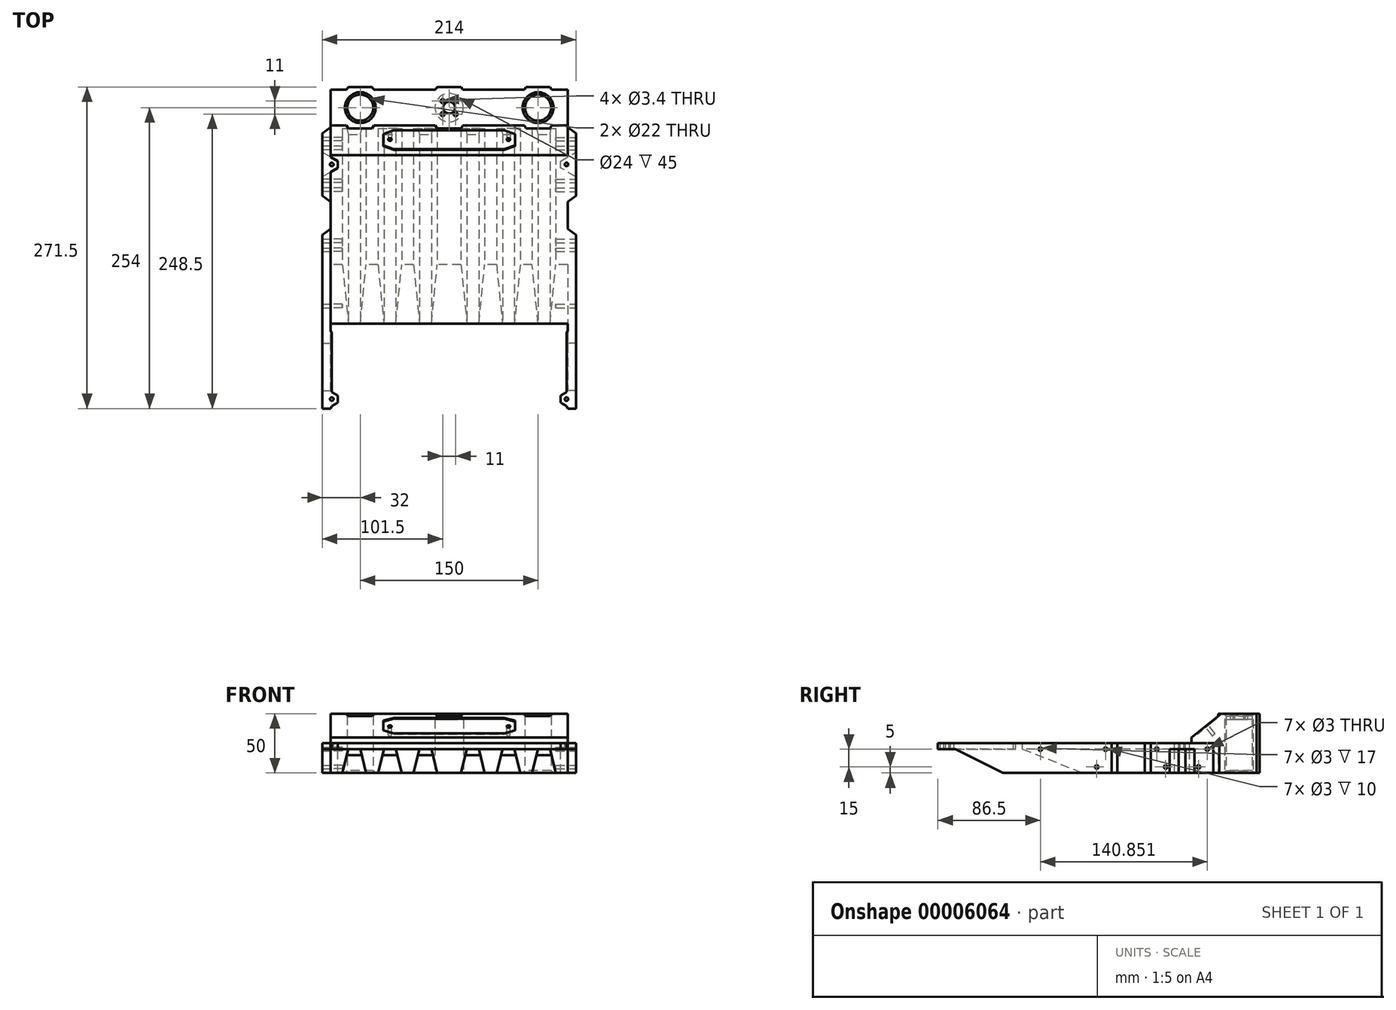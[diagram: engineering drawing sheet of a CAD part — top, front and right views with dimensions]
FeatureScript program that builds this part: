
annotation { "Feature Type Name" : "Feature", "Feature Type Description" : "" }
export const myFeature = defineFeature(function(context is Context, id is Id, definition is map)
    precondition{}
    {
        {
            var Q0;
            Q0=qCreatedBy(makeId("Top.planeOp"),FACE);
            var sketch = newSketch(context, id + "F0", { "sketchPlane" : qUnion([Q0])});
            skLineSegment(sketch, "E0.bottom", {"start": v(0, 0) * mm, "end": v(200, 0) * mm});
            skLineSegment(sketch, "E0.top", {"start": v(0, 30) * mm, "end": v(200, 30) * mm});
            skLineSegment(sketch, "E0.left", {"start": v(0, 0) * mm, "end": v(0, 30) * mm});
            skLineSegment(sketch, "E0.right", {"start": v(200, 0) * mm, "end": v(200, 30) * mm});
            skLineSegment(sketch, "E1", {"start": v(0, 15) * mm, "end": v(200, 15) * mm, "construction": true});
            skLineSegment(sketch, "E2", {"start": v(100, 30) * mm, "end": v(100, 0) * mm, "construction": true});
            skCircle(sketch, "E3", {"center": v(25, 15) * mm, "radius": 11 * mm});
            skCircle(sketch, "E4", {"center": v(175, 15) * mm, "radius": 11 * mm});
            skCircle(sketch, "E5", {"center": v(100, 15) * mm, "radius": 5 * mm});
            skCircle(sketch, "E6.cCircle", {"center": v(25, 15) * mm, "radius": 17.5 * mm, "construction": true});
            skLineSegment(sketch, "E6.0", {"start": v(35.1, -2.5) * mm, "end": v(14.9, -2.5) * mm});
            skLineSegment(sketch, "E6.1", {"start": v(14.9, -2.5) * mm, "end": v(4.8, 15) * mm});
            skLineSegment(sketch, "E6.2", {"start": v(4.8, 15) * mm, "end": v(14.9, 32.5) * mm});
            skLineSegment(sketch, "E6.3", {"start": v(14.9, 32.5) * mm, "end": v(35.1, 32.5) * mm});
            skLineSegment(sketch, "E6.4", {"start": v(35.1, 32.5) * mm, "end": v(45.2, 15) * mm});
            skLineSegment(sketch, "E6.5", {"start": v(45.2, 15) * mm, "end": v(35.1, -2.5) * mm});
            skPoint(sketch, "E6.0.midPoint", {"position": v(25, -2.5) * mm});
            skCircle(sketch, "E7.cCircle", {"center": v(175, 15) * mm, "radius": 17.5 * mm, "construction": true});
            skLineSegment(sketch, "E7.0", {"start": v(164.9, 32.5) * mm, "end": v(185.1, 32.5) * mm});
            skLineSegment(sketch, "E7.1", {"start": v(185.1, 32.5) * mm, "end": v(195.2, 15) * mm});
            skLineSegment(sketch, "E7.2", {"start": v(195.2, 15) * mm, "end": v(185.1, -2.5) * mm});
            skLineSegment(sketch, "E7.3", {"start": v(185.1, -2.5) * mm, "end": v(164.9, -2.5) * mm});
            skLineSegment(sketch, "E7.4", {"start": v(164.9, -2.5) * mm, "end": v(154.8, 15) * mm});
            skLineSegment(sketch, "E7.5", {"start": v(154.8, 15) * mm, "end": v(164.9, 32.5) * mm});
            skPoint(sketch, "E7.0.midPoint", {"position": v(175, 32.5) * mm});
            skLineSegment(sketch, "E8.rect.bottom", {"start": v(94.5, 20.5) * mm, "end": v(105.5, 20.5) * mm, "construction": true});
            skLineSegment(sketch, "E8.rect.top", {"start": v(94.5, 9.5) * mm, "end": v(105.5, 9.5) * mm, "construction": true});
            skLineSegment(sketch, "E8.rect.left", {"start": v(94.5, 20.5) * mm, "end": v(94.5, 9.5) * mm, "construction": true});
            skLineSegment(sketch, "E8.rect.right", {"start": v(105.5, 20.5) * mm, "end": v(105.5, 9.5) * mm, "construction": true});
            skCircle(sketch, "E9", {"center": v(94.5, 20.5) * mm, "radius": 1.7 * mm});
            skCircle(sketch, "E10", {"center": v(105.5, 20.5) * mm, "radius": 1.7 * mm});
            skCircle(sketch, "E11", {"center": v(105.5, 9.5) * mm, "radius": 1.7 * mm});
            skCircle(sketch, "E12", {"center": v(94.5, 9.5) * mm, "radius": 1.7 * mm});
            skCircle(sketch, "E13", {"center": v(100, 15) * mm, "radius": 10.5 * mm});
            skCircle(sketch, "E14.cCircle", {"center": v(100, 15) * mm, "radius": 17.5 * mm, "construction": true});
            skLineSegment(sketch, "E14.0", {"start": v(89.9, 32.5) * mm, "end": v(110.1, 32.5) * mm});
            skLineSegment(sketch, "E14.1", {"start": v(110.1, 32.5) * mm, "end": v(120.2, 15) * mm});
            skLineSegment(sketch, "E14.2", {"start": v(120.2, 15) * mm, "end": v(110.1, -2.5) * mm});
            skLineSegment(sketch, "E14.3", {"start": v(110.1, -2.5) * mm, "end": v(89.9, -2.5) * mm});
            skLineSegment(sketch, "E14.4", {"start": v(89.9, -2.5) * mm, "end": v(79.8, 15) * mm});
            skLineSegment(sketch, "E14.5", {"start": v(79.8, 15) * mm, "end": v(89.9, 32.5) * mm});
            skPoint(sketch, "E14.0.midPoint", {"position": v(100, 32.5) * mm});
            skSolve(sketch);
        }
        {
            var Q0;
            {var subQ7=sQuery(id+"F0.wireOp",EDGE,"E0.left");Q0=makeQuery(id+"F0.imprint","IMPRINT",FACE,{"disambiguationData":[TD([[makeQuery(id+"F0.imprint","IMPRINT",EDGE,{"derivedFrom":subQ7}),-1.0]])]});}
            var Q1;
            {var subQ3=sQuery(id+"F0.wireOp",EDGE,"E6.0");Q1=makeQuery(id+"F0.imprint","IMPRINT",FACE,{"disambiguationData":[TD([[makeQuery(id+"F0.imprint","IMPRINT",EDGE,{"derivedFrom":subQ3}),-1.0]])]});}
            var Q2;
            {var subQ3=sQuery(id+"F0.wireOp",EDGE,"E14.3");Q2=makeQuery(id+"F0.imprint","IMPRINT",FACE,{"disambiguationData":[TD([[makeQuery(id+"F0.imprint","IMPRINT",EDGE,{"derivedFrom":subQ3}),-1.0]])]});}
            var Q3;
            {var subQ3=sQuery(id+"F0.wireOp",EDGE,"E7.3");Q3=makeQuery(id+"F0.imprint","IMPRINT",FACE,{"disambiguationData":[TD([[makeQuery(id+"F0.imprint","IMPRINT",EDGE,{"derivedFrom":subQ3}),-1.0]])]});}
            var Q4;
            {var subQ7=sQuery(id+"F0.wireOp",EDGE,"E0.right");Q4=makeQuery(id+"F0.imprint","IMPRINT",FACE,{"disambiguationData":[TD([[makeQuery(id+"F0.imprint","IMPRINT",EDGE,{"derivedFrom":subQ7}),1.0]])]});}
            var Q5;
            {var subQ0=sQuery(id+"F0.wireOp",EDGE,"E6.3");Q5=makeQuery(id+"F0.imprint","IMPRINT",FACE,{"disambiguationData":[TD([[makeQuery(id+"F0.imprint","IMPRINT",EDGE,{"derivedFrom":subQ0}),-1.0]])]});}
            var Q6;
            {var subQ3=sQuery(id+"F0.wireOp",EDGE,"E14.0");Q6=makeQuery(id+"F0.imprint","IMPRINT",FACE,{"disambiguationData":[TD([[makeQuery(id+"F0.imprint","IMPRINT",EDGE,{"derivedFrom":subQ3}),-1.0]])]});}
            var Q7;
            {var subQ3=sQuery(id+"F0.wireOp",EDGE,"E7.0");Q7=makeQuery(id+"F0.imprint","IMPRINT",FACE,{"disambiguationData":[TD([[makeQuery(id+"F0.imprint","IMPRINT",EDGE,{"derivedFrom":subQ3}),-1.0]])]});}
            var Q8;
            {var subQ5=sQuery(id+"F0.wireOp",EDGE,"E0.bottom");var subQ7=sQuery(id+"F0.wireOp",EDGE,"E6.5");var subQ8=makeQuery(id+"F0.imprint","INTERSECT",VERTEX,{"derivedFrom":[subQ5,subQ7]});Q8=makeQuery(id+"F0.imprint","IMPRINT",FACE,{"disambiguationData":[TD([[makeQuery(id+"F0.imprint","IMPRINT",EDGE,{"disambiguationData":[TD([[subQ8,-1.0]])],"derivedFrom":subQ5}),1.0]])]});}
            var Q9;
            {var subQ0=sQuery(id+"F0.wireOp",EDGE,"E14.2");var subQ1=sQuery(id+"F0.wireOp",EDGE,"E0.bottom");var subQ2=makeQuery(id+"F0.imprint","INTERSECT",VERTEX,{"derivedFrom":[subQ1,subQ0]});Q9=makeQuery(id+"F0.imprint","IMPRINT",FACE,{"disambiguationData":[TD([[makeQuery(id+"F0.imprint","IMPRINT",EDGE,{"disambiguationData":[TD([[subQ2,-1.0]])],"derivedFrom":subQ1}),1.0]])]});}
            var Q10;
            Q10=makeQuery(id+"F0.imprint","IMPRINT",FACE,{"disambiguationData":[TD([[makeQuery(id+"F0.imprint","IMPRINT",EDGE,{"derivedFrom":sQuery(id+"F0.wireOp",EDGE,"E3")}),-1.0]])]});
            var Q11;
            Q11=makeQuery(id+"F0.imprint","IMPRINT",FACE,{"disambiguationData":[TD([[makeQuery(id+"F0.imprint","IMPRINT",EDGE,{"derivedFrom":sQuery(id+"F0.wireOp",EDGE,"E4")}),-1.0]])]});
            var Q12;
            Q12=makeQuery(id+"F0.imprint","IMPRINT",FACE,{"disambiguationData":[TD([[makeQuery(id+"F0.imprint","IMPRINT",EDGE,{"derivedFrom":sQuery(id+"F0.wireOp",EDGE,"E5")}),-1.0]])]});
            var Q13;
            Q13=makeQuery(id+"F0.imprint","IMPRINT",FACE,{"disambiguationData":[TD([[makeQuery(id+"F0.imprint","IMPRINT",EDGE,{"derivedFrom":sQuery(id+"F0.wireOp",EDGE,"E13")}),-1.0]])]});
            extrude(context, id + "F1", {"entities" : qUnion([Q0, Q1, Q2, Q3, Q4, Q5, Q6, Q7, Q8, Q9, Q10, Q11, Q12, Q13]), "depth" : 50 * mm});
        }
        {
            var Q0;
            Q0=makeQuery(id+"F3cPuwSrSVjTx2P_1.boolean.opBoolean","MERGE",FACE,{"derivedFrom":[makeQuery(id+"F1.opExtrude","CAP_FACE",FACE,{"disambiguationData":[OSD([sQuery(id+"F0.wireOp",EDGE,"E0.bottom"),sQuery(id+"F0.wireOp",EDGE,"E0.top"),sQuery(id+"F0.wireOp",EDGE,"E0.left"),sQuery(id+"F0.wireOp",EDGE,"E0.right"),sQuery(id+"F0.wireOp",EDGE,"E3"),sQuery(id+"F0.wireOp",EDGE,"E4"),sQuery(id+"F0.wireOp",EDGE,"E5"),sQuery(id+"F0.wireOp",EDGE,"E6.0"),sQuery(id+"F0.wireOp",EDGE,"E6.1"),sQuery(id+"F0.wireOp",EDGE,"E6.2"),sQuery(id+"F0.wireOp",EDGE,"E6.3"),sQuery(id+"F0.wireOp",EDGE,"E6.4"),sQuery(id+"F0.wireOp",EDGE,"E6.5"),sQuery(id+"F0.wireOp",EDGE,"E7.0"),sQuery(id+"F0.wireOp",EDGE,"E7.1"),sQuery(id+"F0.wireOp",EDGE,"E7.2"),sQuery(id+"F0.wireOp",EDGE,"E7.3"),sQuery(id+"F0.wireOp",EDGE,"E7.4"),sQuery(id+"F0.wireOp",EDGE,"E7.5"),sQuery(id+"F0.wireOp",EDGE,"E9"),sQuery(id+"F0.wireOp",EDGE,"E10"),sQuery(id+"F0.wireOp",EDGE,"E11"),sQuery(id+"F0.wireOp",EDGE,"E12"),sQuery(id+"F0.wireOp",EDGE,"E14.0"),sQuery(id+"F0.wireOp",EDGE,"E14.1"),sQuery(id+"F0.wireOp",EDGE,"E14.2"),sQuery(id+"F0.wireOp",EDGE,"E14.3"),sQuery(id+"F0.wireOp",EDGE,"E14.4"),sQuery(id+"F0.wireOp",EDGE,"E14.5")])],"isStart":true}),makeQuery(id+"F3cPuwSrSVjTx2P_1.opExtrude","SWEPT_FACE",FACE,{"disambiguationData":[OSD([sQuery(id+"F5.wireOp",EDGE,"E16.bottom")])]})]});
            var sketch = newSketch(context, id + "F2", { "sketchPlane" : qUnion([Q0])});
            skCircle(sketch, "E15", {"center": v(100, -15) * mm, "radius": 12 * mm});
            skSolve(sketch);
        }
        {
            var Q0;
            Q0 = qSketchRegion(id + "F2", true);
            extrude(context, id + "F3", {"entities" : qUnion([Q0]), "operationType" : NewBodyOperationType.REMOVE, "oppositeDirection" : true, "depth" : 45 * mm});
        }
        {
            var Q0;
            Q0=makeQuery(id+"F3.boolean.opBoolean","COPY",EDGE,{"derivedFrom":makeQuery(id+"F3.opExtrude","CAP_EDGE",EDGE,{"disambiguationData":[OSD([sQuery(id+"F2.wireOp",EDGE,"E15")])],"isStart":true})});
            var Q1;
            Q1=makeQuery(id+"F1.opExtrude","CAP_EDGE",EDGE,{"disambiguationData":[OSD([sQuery(id+"F0.wireOp",EDGE,"E3")])],"isStart":true});
            var Q2;
            Q2=makeQuery(id+"F1.opExtrude","CAP_EDGE",EDGE,{"disambiguationData":[OSD([sQuery(id+"F0.wireOp",EDGE,"E4")])],"isStart":true});
            var Q3;
            Q3=makeQuery(id+"F1.opExtrude","CAP_EDGE",EDGE,{"disambiguationData":[OSD([sQuery(id+"F0.wireOp",EDGE,"E4")])],"isStart":false});
            var Q4;
            Q4=makeQuery(id+"F1.opExtrude","CAP_EDGE",EDGE,{"disambiguationData":[OSD([sQuery(id+"F0.wireOp",EDGE,"E3")])],"isStart":false});
            chamfer(context, id + "F4", {"entities" : qUnion([Q0, Q1, Q2, Q3, Q4]), "width" : 2 * mm, "tangentPropagation" : true});
        }
        {
            var Q0;
            Q0=qCreatedBy(makeId("Right.planeOp"),FACE);
            var sketch = newSketch(context, id + "F5", { "sketchPlane" : qUnion([Q0])});
            skLineSegment(sketch, "E16.left", {"start": v(0, 0) * mm, "end": v(0, 50) * mm});
            skLineSegment(sketch, "E17", {"start": v(-25, 58.7) * mm, "end": v(-25, -8.7) * mm, "construction": true});
            skLineSegment(sketch, "E18", {"start": v(-117.5, -7.37) * mm, "end": v(-117.5, 57.68) * mm, "construction": true});
            skLineSegment(sketch, "E19", {"start": v(-25, 25) * mm, "end": v(-167.5, 25) * mm});
            skLineSegment(sketch, "E20", {"start": v(-25, 30) * mm, "end": v(-25, 25) * mm});
            skLineSegment(sketch, "E21", {"start": v(-167.5, 20) * mm, "end": v(-167.5, 25) * mm});
            skLineSegment(sketch, "E22", {"start": v(-25, 0) * mm, "end": v(0, 0) * mm});
            skLineSegment(sketch, "E23", {"start": v(-25, 0) * mm, "end": v(-117.5, 0) * mm});
            skLineSegment(sketch, "E24", {"start": v(-117.5, 0) * mm, "end": v(-167.5, 20) * mm});
            skLineSegment(sketch, "E25", {"start": v(-25, 30) * mm, "end": v(0, 50) * mm});
            skLineSegment(sketch, "E26", {"start": v(0, 50) * mm, "end": v(0, 47) * mm, "construction": true});
            skSolve(sketch);
        }
        {
            var Q0;
            {var subQ6=sQuery(id+"F5.wireOp",EDGE,"E16.left");Q0=makeQuery(id+"F5.imprint","IMPRINT",FACE,{"disambiguationData":[TD([[makeQuery(id+"F5.imprint","IMPRINT",EDGE,{"derivedFrom":subQ6}),1.0]])]});}
            extrude(context, id + "F6", {"entities" : qUnion([Q0]), "operationType" : NewBodyOperationType.ADD, "depth" : 200 * mm});
        }
        {
            var Q0;
            Q0=makeQuery(id+"F6.opExtrude","SWEPT_FACE",FACE,{"disambiguationData":[OSD([sQuery(id+"F5.wireOp",EDGE,"E21")])]});
            var sketch = newSketch(context, id + "F7", { "sketchPlane" : qUnion([Q0])});
            skLineSegment(sketch, "E27.bottom", {"start": v(0, 20) * mm, "end": v(200, 20) * mm});
            skLineSegment(sketch, "E27.top", {"start": v(0, 0) * mm, "end": v(200, 0) * mm});
            skLineSegment(sketch, "E27.left", {"start": v(0, 20) * mm, "end": v(0, 0) * mm});
            skLineSegment(sketch, "E27.right", {"start": v(200, 20) * mm, "end": v(200, 0) * mm});
            skLineSegment(sketch, "E28", {"start": v(0, 0) * mm, "end": v(10, 0) * mm});
            skLineSegment(sketch, "E29", {"start": v(10, 0) * mm, "end": v(15, 20) * mm});
            skLineSegment(sketch, "E30", {"start": v(15, 20) * mm, "end": v(0, 20) * mm});
            skLineSegment(sketch, "E31", {"start": v(200, 20) * mm, "end": v(185, 20) * mm});
            skLineSegment(sketch, "E32", {"start": v(185, 20) * mm, "end": v(190, 0) * mm});
            skLineSegment(sketch, "E33", {"start": v(190, 0) * mm, "end": v(200, 0) * mm});
            skLineSegment(sketch, "E34", {"start": v(25, 20) * mm, "end": v(30, 0) * mm});
            skLineSegment(sketch, "E35", {"start": v(40, 0) * mm, "end": v(45, 20) * mm});
            skLineSegment(sketch, "E36", {"start": v(175, 20) * mm, "end": v(170, 0) * mm});
            skLineSegment(sketch, "E37", {"start": v(160, 0) * mm, "end": v(155, 20) * mm});
            skLineSegment(sketch, "E38", {"start": v(140, 0) * mm, "end": v(145, 20) * mm});
            skLineSegment(sketch, "E39", {"start": v(55, 20) * mm, "end": v(60, 0) * mm});
            skLineSegment(sketch, "E40", {"start": v(70, 0) * mm, "end": v(75, 20) * mm});
            skLineSegment(sketch, "E41", {"start": v(85, 20) * mm, "end": v(90, 0) * mm});
            skLineSegment(sketch, "E42", {"start": v(110, 0) * mm, "end": v(115, 20) * mm});
            skLineSegment(sketch, "E43", {"start": v(125, 20) * mm, "end": v(130, 0) * mm});
            skSolve(sketch);
        }
        {
            var Q0;
            {var subQ2=sQuery(id+"F7.wireOp",EDGE,"E29");Q0=makeQuery(id+"F7.imprint","IMPRINT",FACE,{"disambiguationData":[TD([[makeQuery(id+"F7.imprint","IMPRINT",EDGE,{"derivedFrom":subQ2}),-1.0]])]});}
            var Q1;
            {var subQ1=sQuery(id+"F7.wireOp",EDGE,"E35");Q1=makeQuery(id+"F7.imprint","IMPRINT",FACE,{"disambiguationData":[TD([[makeQuery(id+"F7.imprint","IMPRINT",EDGE,{"derivedFrom":subQ1}),-1.0]])]});}
            var Q2;
            {var subQ1=sQuery(id+"F7.wireOp",EDGE,"E40");Q2=makeQuery(id+"F7.imprint","IMPRINT",FACE,{"disambiguationData":[TD([[makeQuery(id+"F7.imprint","IMPRINT",EDGE,{"derivedFrom":subQ1}),-1.0]])]});}
            var Q3;
            {var subQ1=sQuery(id+"F7.wireOp",EDGE,"E42");Q3=makeQuery(id+"F7.imprint","IMPRINT",FACE,{"disambiguationData":[TD([[makeQuery(id+"F7.imprint","IMPRINT",EDGE,{"derivedFrom":subQ1}),-1.0]])]});}
            var Q4;
            {var subQ1=sQuery(id+"F7.wireOp",EDGE,"E37");Q4=makeQuery(id+"F7.imprint","IMPRINT",FACE,{"disambiguationData":[TD([[makeQuery(id+"F7.imprint","IMPRINT",EDGE,{"derivedFrom":subQ1}),1.0]])]});}
            var Q5;
            {var subQ1=sQuery(id+"F7.wireOp",EDGE,"E32");Q5=makeQuery(id+"F7.imprint","IMPRINT",FACE,{"disambiguationData":[TD([[makeQuery(id+"F7.imprint","IMPRINT",EDGE,{"derivedFrom":subQ1}),-1.0]])]});}
            extrude(context, id + "F8", {"entities" : qUnion([Q0, Q1, Q2, Q3, Q4, Q5]), "operationType" : NewBodyOperationType.REMOVE, "oppositeDirection" : true, "depth" : 165 * mm});
        }
        {
            var Q0;
            {var subQ0=sQuery(id+"F7.wireOp",EDGE,"E27.bottom");Q0=makeQuery(id+"F8.boolean.opBoolean","COPY",EDGE,{"derivedFrom":makeQuery(id+"F8.opExtrude","CAP_EDGE",EDGE,{"disambiguationData":[OSD([subQ0]),TDD([makeQuery(id+"F7.imprint","IMPRINT",EDGE,{"disambiguationData":[TD([[makeQuery(id+"F7.imprint","INTERSECT",VERTEX,{"derivedFrom":[subQ0,sQuery(id+"F7.wireOp",EDGE,"E34")]}),-1.0]])],"derivedFrom":subQ0})])],"isStart":false})});}
            var Q1;
            {var subQ0=sQuery(id+"F7.wireOp",EDGE,"E27.bottom");Q1=makeQuery(id+"F8.boolean.opBoolean","COPY",EDGE,{"derivedFrom":makeQuery(id+"F8.opExtrude","CAP_EDGE",EDGE,{"disambiguationData":[OSD([subQ0]),TDD([makeQuery(id+"F7.imprint","IMPRINT",EDGE,{"disambiguationData":[TD([[makeQuery(id+"F7.imprint","INTERSECT",VERTEX,{"derivedFrom":[subQ0,sQuery(id+"F7.wireOp",EDGE,"E35")]}),1.0]])],"derivedFrom":subQ0})])],"isStart":false})});}
            var Q2;
            {var subQ0=sQuery(id+"F7.wireOp",EDGE,"E27.bottom");Q2=makeQuery(id+"F8.boolean.opBoolean","COPY",EDGE,{"derivedFrom":makeQuery(id+"F8.opExtrude","CAP_EDGE",EDGE,{"disambiguationData":[OSD([subQ0]),TDD([makeQuery(id+"F7.imprint","IMPRINT",EDGE,{"disambiguationData":[TD([[makeQuery(id+"F7.imprint","INTERSECT",VERTEX,{"derivedFrom":[subQ0,sQuery(id+"F7.wireOp",EDGE,"E40")]}),1.0]])],"derivedFrom":subQ0})])],"isStart":false})});}
            var Q3;
            {var subQ0=sQuery(id+"F7.wireOp",EDGE,"E27.bottom");Q3=makeQuery(id+"F8.boolean.opBoolean","COPY",EDGE,{"derivedFrom":makeQuery(id+"F8.opExtrude","CAP_EDGE",EDGE,{"disambiguationData":[OSD([subQ0]),TDD([makeQuery(id+"F7.imprint","IMPRINT",EDGE,{"disambiguationData":[TD([[makeQuery(id+"F7.imprint","INTERSECT",VERTEX,{"derivedFrom":[subQ0,sQuery(id+"F7.wireOp",EDGE,"E42")]}),1.0]])],"derivedFrom":subQ0})])],"isStart":false})});}
            var Q4;
            {var subQ0=sQuery(id+"F7.wireOp",EDGE,"E27.bottom");Q4=makeQuery(id+"F8.boolean.opBoolean","COPY",EDGE,{"derivedFrom":makeQuery(id+"F8.opExtrude","CAP_EDGE",EDGE,{"disambiguationData":[OSD([subQ0]),TDD([makeQuery(id+"F7.imprint","IMPRINT",EDGE,{"disambiguationData":[TD([[makeQuery(id+"F7.imprint","INTERSECT",VERTEX,{"derivedFrom":[subQ0,sQuery(id+"F7.wireOp",EDGE,"E37")]}),-1.0]])],"derivedFrom":subQ0})])],"isStart":false})});}
            var Q5;
            {var subQ0=sQuery(id+"F7.wireOp",EDGE,"E27.bottom");Q5=makeQuery(id+"F8.boolean.opBoolean","COPY",EDGE,{"derivedFrom":makeQuery(id+"F8.opExtrude","CAP_EDGE",EDGE,{"disambiguationData":[OSD([subQ0]),TDD([makeQuery(id+"F7.imprint","IMPRINT",EDGE,{"disambiguationData":[TD([[makeQuery(id+"F7.imprint","INTERSECT",VERTEX,{"derivedFrom":[subQ0,sQuery(id+"F7.wireOp",EDGE,"E36")]}),1.0]])],"derivedFrom":subQ0})])],"isStart":false})});}
            chamfer(context, id + "F9", {"entities" : qUnion([Q0, Q1, Q2, Q3, Q4, Q5]), "width" : 5 * mm, "tangentPropagation" : true});
        }
        {
            var Q0;
            Q0=makeQuery(id+"F6.opExtrude","SWEPT_FACE",FACE,{"disambiguationData":[OSD([sQuery(id+"F5.wireOp",EDGE,"E25")])]});
            var sketch = newSketch(context, id + "F10", { "sketchPlane" : qUnion([Q0])});
            skLineSegment(sketch, "E44.bottom", {"start": v(0, 31.23) * mm, "end": v(200, 31.23) * mm, "construction": true});
            skLineSegment(sketch, "E44.top", {"start": v(0, -0.78) * mm, "end": v(200, -0.78) * mm, "construction": true});
            skLineSegment(sketch, "E44.left", {"start": v(0, 31.23) * mm, "end": v(0, -0.78) * mm, "construction": true});
            skLineSegment(sketch, "E44.right", {"start": v(200, 31.23) * mm, "end": v(200, -0.78) * mm, "construction": true});
            skLineSegment(sketch, "E45", {"start": v(0, 15.23) * mm, "end": v(200, 15.23) * mm, "construction": true});
            skCircle(sketch, "E46", {"center": v(50, 15.23) * mm, "radius": 1.5 * mm});
            skCircle(sketch, "E47", {"center": v(150, 15.23) * mm, "radius": 1.5 * mm});
            skSolve(sketch);
        }
        {
            var Q0;
            Q0 = qSketchRegion(id + "F10", true);
            extrude(context, id + "F11", {"entities" : qUnion([Q0]), "operationType" : NewBodyOperationType.REMOVE, "oppositeDirection" : true, "depth" : 10 * mm});
        }
        {
            var Q0;
            Q0=makeQuery(id+"F6.opExtrude","SWEPT_FACE",FACE,{"disambiguationData":[OSD([sQuery(id+"F5.wireOp",EDGE,"E25")])]});
            var sketch = newSketch(context, id + "F12", { "sketchPlane" : qUnion([Q0])});
            skLineSegment(sketch, "E48.bottom", {"start": v(0, 31.23) * mm, "end": v(200, 31.23) * mm, "construction": true});
            skLineSegment(sketch, "E48.top", {"start": v(0, -0.78) * mm, "end": v(200, -0.78) * mm, "construction": true});
            skLineSegment(sketch, "E48.left", {"start": v(0, 31.23) * mm, "end": v(0, -0.78) * mm, "construction": true});
            skLineSegment(sketch, "E48.right", {"start": v(200, 31.23) * mm, "end": v(200, -0.78) * mm, "construction": true});
            skLineSegment(sketch, "E49", {"start": v(0, 15.23) * mm, "end": v(200, 15.23) * mm, "construction": true});
            skLineSegment(sketch, "E50.bottom", {"start": v(44.5, 25.73) * mm, "end": v(155.5, 25.73) * mm});
            skLineSegment(sketch, "E50.top", {"start": v(44.5, 4.73) * mm, "end": v(155.5, 4.73) * mm});
            skLineSegment(sketch, "E50.left", {"start": v(44.5, 25.73) * mm, "end": v(44.5, 4.73) * mm});
            skLineSegment(sketch, "E50.right", {"start": v(155.5, 25.73) * mm, "end": v(155.5, 4.73) * mm});
            skSolve(sketch);
        }
        {
            var Q0;
            Q0 = qSketchRegion(id + "F12", true);
            extrude(context, id + "F13", {"entities" : qUnion([Q0]), "operationType" : NewBodyOperationType.REMOVE, "oppositeDirection" : true, "depth" : 1 * mm});
        }
        {
            var Q0;
            Q0=makeQuery(id+"F13.boolean.opBoolean","COPY",EDGE,{"derivedFrom":makeQuery(id+"F13.opExtrude","SWEPT_EDGE",EDGE,{"disambiguationData":[OSD([sQuery(id+"F12.wireOp",EDGE,"E50.bottom"),sQuery(id+"F12.wireOp",EDGE,"E50.left")])]})});
            var Q1;
            Q1=makeQuery(id+"F13.boolean.opBoolean","COPY",EDGE,{"derivedFrom":makeQuery(id+"F13.opExtrude","SWEPT_EDGE",EDGE,{"disambiguationData":[OSD([sQuery(id+"F12.wireOp",EDGE,"E50.bottom"),sQuery(id+"F12.wireOp",EDGE,"E50.right")])]})});
            var Q2;
            Q2=makeQuery(id+"F13.boolean.opBoolean","COPY",EDGE,{"derivedFrom":makeQuery(id+"F13.opExtrude","SWEPT_EDGE",EDGE,{"disambiguationData":[OSD([sQuery(id+"F12.wireOp",EDGE,"E50.top"),sQuery(id+"F12.wireOp",EDGE,"E50.right")])]})});
            var Q3;
            Q3=makeQuery(id+"F13.boolean.opBoolean","COPY",EDGE,{"derivedFrom":makeQuery(id+"F13.opExtrude","SWEPT_EDGE",EDGE,{"disambiguationData":[OSD([sQuery(id+"F12.wireOp",EDGE,"E50.top"),sQuery(id+"F12.wireOp",EDGE,"E50.left")])]})});
            chamfer(context, id + "F14", {"entities" : qUnion([Q0, Q1, Q2, Q3]), "chamferType" : ChamferType.TWO_OFFSETS, "width1" : 4 * mm, "oppositeDirection" : false, "width2" : 9 * mm, "tangentPropagation" : true});
        }
        {
            var Q0;
            Q0=makeQuery(id+"F6.boolean.opBoolean","MERGE",FACE,{"derivedFrom":[makeQuery(id+"F1.opExtrude","SWEPT_FACE",FACE,{"disambiguationData":[OSD([sQuery(id+"F0.wireOp",EDGE,"E0.right")])]}),makeQuery(id+"F6.opExtrude","CAP_FACE",FACE,{"disambiguationData":[OSD([sQuery(id+"F5.wireOp",EDGE,"E16.left"),sQuery(id+"F5.wireOp",EDGE,"E19"),sQuery(id+"F5.wireOp",EDGE,"E20"),sQuery(id+"F5.wireOp",EDGE,"E21"),sQuery(id+"F5.wireOp",EDGE,"E22"),sQuery(id+"F5.wireOp",EDGE,"E23"),sQuery(id+"F5.wireOp",EDGE,"E24"),sQuery(id+"F5.wireOp",EDGE,"E25")])],"isStart":false})]});
            var sketch = newSketch(context, id + "F15", { "sketchPlane" : qUnion([Q0])});
            skLineSegment(sketch, "E51", {"start": v(-92.5, 0) * mm, "end": v(-117.5, 0) * mm});
            skLineSegment(sketch, "E52", {"start": v(-117.5, 0) * mm, "end": v(-184, 0) * mm});
            skLineSegment(sketch, "E53", {"start": v(-239, 20) * mm, "end": v(-239, 25) * mm});
            skLineSegment(sketch, "E54", {"start": v(-239, 25) * mm, "end": v(-92.5, 25) * mm});
            skLineSegment(sketch, "E55", {"start": v(-92.5, 25) * mm, "end": v(-92.5, 0) * mm, "construction": true});
            skCircle(sketch, "E56", {"center": v(-97.5, 20) * mm, "radius": 1.5 * mm});
            skCircle(sketch, "E57", {"center": v(-152.5, 20) * mm, "radius": 1.5 * mm});
            skLineSegment(sketch, "E58", {"start": v(-105, 0) * mm, "end": v(-105, 25) * mm, "construction": true});
            skCircle(sketch, "E59", {"center": v(-105, 5) * mm, "radius": 1.5 * mm});
            skLineSegment(sketch, "E60", {"start": v(-92.5, 25) * mm, "end": v(-87.5, 25) * mm});
            skLineSegment(sketch, "E61", {"start": v(-239, 20) * mm, "end": v(-224, 20) * mm});
            skLineSegment(sketch, "E62", {"start": v(-224, 20) * mm, "end": v(-184, 0) * mm});
            skLineSegment(sketch, "E63", {"start": v(-87.5, 25) * mm, "end": v(-87.5, 0) * mm});
            skLineSegment(sketch, "E64", {"start": v(-87.5, 0) * mm, "end": v(-92.5, 0) * mm});
            skSolve(sketch);
        }
        {
            var Q0;
            Q0 = qSketchRegion(id + "F15", true);
            extrude(context, id + "F16", {"entities" : qUnion([Q0]), "depth" : 7 * mm});
        }
        {
            var Q0;
            Q0=makeQuery(id+"F15.imprint","IMPRINT",FACE,{"disambiguationData":[TD([[makeQuery(id+"F15.imprint","IMPRINT",EDGE,{"derivedFrom":sQuery(id+"F15.wireOp",EDGE,"E57")}),1.0]])]});
            var Q1;
            Q1=makeQuery(id+"F15.imprint","IMPRINT",FACE,{"disambiguationData":[TD([[makeQuery(id+"F15.imprint","IMPRINT",EDGE,{"derivedFrom":sQuery(id+"F15.wireOp",EDGE,"E59")}),1.0]])]});
            var Q2;
            Q2=makeQuery(id+"F15.imprint","IMPRINT",FACE,{"disambiguationData":[TD([[makeQuery(id+"F15.imprint","IMPRINT",EDGE,{"derivedFrom":sQuery(id+"F15.wireOp",EDGE,"E56")}),1.0]])]});
            extrude(context, id + "F17", {"entities" : qUnion([Q0, Q1, Q2]), "operationType" : NewBodyOperationType.REMOVE, "oppositeDirection" : true, "depth" : 10 * mm});
        }
        {
            var Q0;
            Q0=makeQuery(id+"F16.opExtrude","SWEPT_FACE",FACE,{"disambiguationData":[OSD([sQuery(id+"F15.wireOp",EDGE,"E54"),sQuery(id+"F15.wireOp",EDGE,"E60")])]});
            var sketch = newSketch(context, id + "F18", { "sketchPlane" : qUnion([Q0])});
            skLineSegment(sketch, "E65.bottom", {"start": v(200, -239) * mm, "end": v(207, -239) * mm, "construction": true});
            skLineSegment(sketch, "E65.top", {"start": v(200, -87.5) * mm, "end": v(207, -87.5) * mm, "construction": true});
            skLineSegment(sketch, "E65.left", {"start": v(200, -239) * mm, "end": v(200, -87.5) * mm, "construction": true});
            skLineSegment(sketch, "E65.right", {"start": v(207, -239) * mm, "end": v(207, -87.5) * mm, "construction": true});
            skLineSegment(sketch, "E66", {"start": v(200, -87.5) * mm, "end": v(200, -92.5) * mm});
            skLineSegment(sketch, "E67", {"start": v(207, -92.5) * mm, "end": v(200, -87.5) * mm});
            skLineSegment(sketch, "E68", {"start": v(207, -92.5) * mm, "end": v(207, -87.5) * mm});
            skLineSegment(sketch, "E69", {"start": v(207, -92.5) * mm, "end": v(200, -92.5) * mm, "construction": true});
            skLineSegment(sketch, "E70", {"start": v(207, -87.5) * mm, "end": v(207, -92.5) * mm});
            skLineSegment(sketch, "E71", {"start": v(207, -87.5) * mm, "end": v(200, -87.5) * mm});
            skLineSegment(sketch, "E72", {"start": v(200, -92.5) * mm, "end": v(200, -87.5) * mm, "construction": true});
            skLineSegment(sketch, "E73", {"start": v(207, -231) * mm, "end": v(185.95, -231) * mm, "construction": true});
            skCircle(sketch, "E74", {"center": v(199, -231) * mm, "radius": 1.5 * mm});
            skCircle(sketch, "E75.cCircle", {"center": v(199, -231) * mm, "radius": 5 * mm, "construction": true});
            skLineSegment(sketch, "E75.0", {"start": v(204, -228.11) * mm, "end": v(204, -233.89) * mm});
            skLineSegment(sketch, "E75.1", {"start": v(204, -233.89) * mm, "end": v(199, -236.77) * mm});
            skLineSegment(sketch, "E75.2", {"start": v(199, -236.77) * mm, "end": v(194, -233.89) * mm});
            skLineSegment(sketch, "E75.3", {"start": v(194, -233.89) * mm, "end": v(194, -228.11) * mm});
            skLineSegment(sketch, "E75.4", {"start": v(194, -228.11) * mm, "end": v(199, -225.23) * mm});
            skLineSegment(sketch, "E75.5", {"start": v(199, -225.23) * mm, "end": v(204, -228.11) * mm});
            skPoint(sketch, "E75.0.midPoint", {"position": v(204, -231) * mm});
            skLineSegment(sketch, "E76", {"start": v(199, -225.23) * mm, "end": v(199, -175.23) * mm});
            skLineSegment(sketch, "E77", {"start": v(199, -175.23) * mm, "end": v(200, -175.23) * mm});
            skLineSegment(sketch, "E78", {"start": v(199, -175.23) * mm, "end": v(200, -173.23) * mm});
            skLineSegment(sketch, "E79", {"start": v(200, -239) * mm, "end": v(199, -236.77) * mm});
            skSolve(sketch);
        }
        {
            var Q0;
            Q0=makeQuery(id+"F18.imprint","IMPRINT",FACE,{"disambiguationData":[TD([[makeQuery(id+"F18.imprint","IMPRINT",EDGE,{"derivedFrom":sQuery(id+"F18.wireOp",EDGE,"E67")}),-1.0]])]});
            var Q1;
            {var subQ0=makeQuery(id+"F16.opExtrude","CAP_EDGE",EDGE,{"disambiguationData":[OSD([sQuery(id+"F15.wireOp",EDGE,"E54"),sQuery(id+"F15.wireOp",EDGE,"E60")])],"isStart":true});var subQ1=sQuery(id+"F18.wireOp",EDGE,"E74");var subQ3=makeQuery(id+"F18.imprint","INTERSECT",VERTEX,{"disambiguationData":[OD(0.0)],"derivedFrom":[subQ0,subQ1]});Q1=makeQuery(id+"F18.imprint","IMPRINT",FACE,{"disambiguationData":[TD([[makeQuery(id+"F18.imprint","IMPRINT",EDGE,{"disambiguationData":[TD([[subQ3,-1.0]])],"derivedFrom":subQ1}),1.0]])]});}
            var Q2;
            {var subQ8=sQuery(id+"F18.wireOp",EDGE,"E75.0");Q2=makeQuery(id+"F18.imprint","IMPRINT",FACE,{"disambiguationData":[TD([[makeQuery(id+"F18.imprint","IMPRINT",EDGE,{"derivedFrom":subQ8}),-1.0]])]});}
            var Q3;
            {var subQ9=sQuery(id+"F18.wireOp",EDGE,"E75.2");Q3=makeQuery(id+"F18.imprint","IMPRINT",FACE,{"disambiguationData":[TD([[makeQuery(id+"F18.imprint","IMPRINT",EDGE,{"derivedFrom":subQ9}),-1.0]])]});}
            var Q4;
            {var subQ5=sQuery(id+"F18.wireOp",EDGE,"4f99f6da-fdaa-4f9a-9e0c-8dcd1be6926c");Q4=makeQuery(id+"F18.imprint","IMPRINT",FACE,{"disambiguationData":[TD([[makeQuery(id+"F18.imprint","IMPRINT",EDGE,{"derivedFrom":subQ5}),1.0]])]});}
            var Q5;
            {var subQ4=sQuery(id+"F18.wireOp",EDGE,"E76");Q5=makeQuery(id+"F18.imprint","IMPRINT",FACE,{"disambiguationData":[TD([[makeQuery(id+"F18.imprint","IMPRINT",EDGE,{"derivedFrom":subQ4}),-1.0]])]});}
            var Q6;
            {var subQ2=sQuery(id+"F18.wireOp",EDGE,"E77");Q6=makeQuery(id+"F18.imprint","IMPRINT",FACE,{"disambiguationData":[TD([[makeQuery(id+"F18.imprint","IMPRINT",EDGE,{"derivedFrom":subQ2}),1.0]])]});}
            var Q7;
            {var subQ4=sQuery(id+"F18.wireOp",EDGE,"E79");Q7=makeQuery(id+"F18.imprint","IMPRINT",FACE,{"disambiguationData":[TD([[makeQuery(id+"F18.imprint","IMPRINT",EDGE,{"derivedFrom":subQ4}),-1.0]])]});}
            extrude(context, id + "F19", {"entities" : qUnion([Q0, Q1, Q2, Q3, Q4, Q5, Q6, Q7]), "operationType" : NewBodyOperationType.ADD, "oppositeDirection" : true, "depth" : 5 * mm});
        }
        {
            var Q0;
            Q0=makeQuery(id+"F18.imprint","IMPRINT",FACE,{"disambiguationData":[TD([[makeQuery(id+"F18.imprint","IMPRINT",EDGE,{"derivedFrom":sQuery(id+"F18.wireOp",EDGE,"E67")}),-1.0]])]});
            var Q1;
            {var subQ0=makeQuery(id+"F16.opExtrude","CAP_EDGE",EDGE,{"disambiguationData":[OSD([sQuery(id+"F15.wireOp",EDGE,"E54"),sQuery(id+"F15.wireOp",EDGE,"E60")])],"isStart":true});var subQ1=sQuery(id+"F18.wireOp",EDGE,"E74");var subQ3=makeQuery(id+"F18.imprint","INTERSECT",VERTEX,{"disambiguationData":[OD(0.0)],"derivedFrom":[subQ0,subQ1]});Q1=makeQuery(id+"F18.imprint","IMPRINT",FACE,{"disambiguationData":[TD([[makeQuery(id+"F18.imprint","IMPRINT",EDGE,{"disambiguationData":[TD([[subQ3,1.0]])],"derivedFrom":subQ1}),1.0]])]});}
            var Q2;
            {var subQ0=makeQuery(id+"F16.opExtrude","CAP_EDGE",EDGE,{"disambiguationData":[OSD([sQuery(id+"F15.wireOp",EDGE,"E54"),sQuery(id+"F15.wireOp",EDGE,"E60")])],"isStart":true});var subQ1=sQuery(id+"F18.wireOp",EDGE,"E74");var subQ3=makeQuery(id+"F18.imprint","INTERSECT",VERTEX,{"disambiguationData":[OD(0.0)],"derivedFrom":[subQ0,subQ1]});Q2=makeQuery(id+"F18.imprint","IMPRINT",FACE,{"disambiguationData":[TD([[makeQuery(id+"F18.imprint","IMPRINT",EDGE,{"disambiguationData":[TD([[subQ3,-1.0]])],"derivedFrom":subQ1}),1.0]])]});}
            extrude(context, id + "F20", {"entities" : qUnion([Q0, Q1, Q2]), "operationType" : NewBodyOperationType.REMOVE, "oppositeDirection" : true, "depth" : 25 * mm});
        }
        {
            var Q0;
            Q0=makeQuery(id+"F6.boolean.opBoolean","MERGE",FACE,{"derivedFrom":[makeQuery(id+"F1.opExtrude","SWEPT_FACE",FACE,{"disambiguationData":[OSD([sQuery(id+"F0.wireOp",EDGE,"E0.left")])]}),makeQuery(id+"F6.opExtrude","CAP_FACE",FACE,{"disambiguationData":[OSD([sQuery(id+"F5.wireOp",EDGE,"E16.left"),sQuery(id+"F5.wireOp",EDGE,"E19"),sQuery(id+"F5.wireOp",EDGE,"E20"),sQuery(id+"F5.wireOp",EDGE,"E21"),sQuery(id+"F5.wireOp",EDGE,"E22"),sQuery(id+"F5.wireOp",EDGE,"E23"),sQuery(id+"F5.wireOp",EDGE,"E24"),sQuery(id+"F5.wireOp",EDGE,"E25")])],"isStart":true})]});
            var sketch = newSketch(context, id + "F21", { "sketchPlane" : qUnion([Q0])});
            skLineSegment(sketch, "E80", {"start": v(92.5, 0) * mm, "end": v(92.5, 25) * mm, "construction": true});
            skLineSegment(sketch, "E81", {"start": v(92.5, 25) * mm, "end": v(239, 25) * mm});
            skLineSegment(sketch, "E82", {"start": v(239, 25) * mm, "end": v(239, 20) * mm});
            skLineSegment(sketch, "E83", {"start": v(239, 20) * mm, "end": v(224, 20) * mm});
            skLineSegment(sketch, "E84", {"start": v(224, 20) * mm, "end": v(184, 0) * mm});
            skLineSegment(sketch, "E85", {"start": v(184, 0) * mm, "end": v(92.5, 0) * mm});
            skPoint(sketch, "E86", {"position": v(117.5, 0) * mm});
            skPoint(sketch, "E87", {"position": v(167.5, 25) * mm});
            skLineSegment(sketch, "E88", {"start": v(92.5, 25) * mm, "end": v(87.5, 25) * mm});
            skLineSegment(sketch, "E89", {"start": v(87.5, 25) * mm, "end": v(87.5, 0) * mm});
            skLineSegment(sketch, "E90", {"start": v(87.5, 0) * mm, "end": v(92.5, 0) * mm});
            skCircle(sketch, "E91", {"center": v(152.5, 20) * mm, "radius": 1.5 * mm});
            skCircle(sketch, "E92", {"center": v(97.5, 20) * mm, "radius": 1.5 * mm});
            skPoint(sketch, "E93", {"position": v(92.5, 0) * mm});
            skLineSegment(sketch, "E94", {"start": v(117.5, 0) * mm, "end": v(92.5, 0) * mm});
            skLineSegment(sketch, "E95", {"start": v(105, 0) * mm, "end": v(105, 25) * mm, "construction": true});
            skCircle(sketch, "E96", {"center": v(105, 5) * mm, "radius": 1.5 * mm});
            skSolve(sketch);
        }
        {
            var Q0;
            Q0 = qSketchRegion(id + "F21", true);
            extrude(context, id + "F22", {"entities" : qUnion([Q0]), "depth" : 7 * mm});
        }
        {
            var Q0;
            Q0=makeQuery(id+"F21.imprint","IMPRINT",FACE,{"disambiguationData":[TD([[makeQuery(id+"F21.imprint","IMPRINT",EDGE,{"derivedFrom":sQuery(id+"F21.wireOp",EDGE,"E92")}),1.0]])]});
            var Q1;
            Q1=makeQuery(id+"F21.imprint","IMPRINT",FACE,{"disambiguationData":[TD([[makeQuery(id+"F21.imprint","IMPRINT",EDGE,{"derivedFrom":sQuery(id+"F21.wireOp",EDGE,"E96")}),1.0]])]});
            var Q2;
            Q2=makeQuery(id+"F21.imprint","IMPRINT",FACE,{"disambiguationData":[TD([[makeQuery(id+"F21.imprint","IMPRINT",EDGE,{"derivedFrom":sQuery(id+"F21.wireOp",EDGE,"E91")}),1.0]])]});
            extrude(context, id + "F23", {"entities" : qUnion([Q0, Q1, Q2]), "operationType" : NewBodyOperationType.REMOVE, "oppositeDirection" : true, "depth" : 10 * mm});
        }
        {
            var Q0;
            Q0=makeQuery(id+"F22.opExtrude","SWEPT_FACE",FACE,{"disambiguationData":[OSD([sQuery(id+"F21.wireOp",EDGE,"E81"),sQuery(id+"F21.wireOp",EDGE,"E88")])]});
            var sketch = newSketch(context, id + "F24", { "sketchPlane" : qUnion([Q0])});
            skLineSegment(sketch, "E97.bottom", {"start": v(-7, -239) * mm, "end": v(0, -239) * mm, "construction": true});
            skLineSegment(sketch, "E97.top", {"start": v(-7, -87.5) * mm, "end": v(0, -87.5) * mm, "construction": true});
            skLineSegment(sketch, "E97.left", {"start": v(-7, -239) * mm, "end": v(-7, -87.5) * mm, "construction": true});
            skLineSegment(sketch, "E97.right", {"start": v(0, -239) * mm, "end": v(0, -87.5) * mm, "construction": true});
            skLineSegment(sketch, "E98", {"start": v(0, -87.5) * mm, "end": v(-7, -92.5) * mm});
            skLineSegment(sketch, "E99", {"start": v(-7, -92.5) * mm, "end": v(0, -92.5) * mm, "construction": true});
            skCircle(sketch, "E100", {"center": v(1, -231) * mm, "radius": 1.5 * mm});
            skCircle(sketch, "E101.cCircle", {"center": v(1, -231) * mm, "radius": 5 * mm, "construction": true});
            skLineSegment(sketch, "E101.0", {"start": v(-4, -233.89) * mm, "end": v(-4, -228.11) * mm});
            skLineSegment(sketch, "E101.1", {"start": v(-4, -228.11) * mm, "end": v(1, -225.23) * mm});
            skLineSegment(sketch, "E101.2", {"start": v(1, -225.23) * mm, "end": v(6, -228.11) * mm});
            skLineSegment(sketch, "E101.3", {"start": v(6, -228.11) * mm, "end": v(6, -233.89) * mm});
            skLineSegment(sketch, "E101.4", {"start": v(6, -233.89) * mm, "end": v(1, -236.77) * mm});
            skLineSegment(sketch, "E101.5", {"start": v(1, -236.77) * mm, "end": v(-4, -233.89) * mm});
            skPoint(sketch, "E101.0.midPoint", {"position": v(-4, -231) * mm});
            skLineSegment(sketch, "E102", {"start": v(0, -239) * mm, "end": v(1, -236.77) * mm});
            skLineSegment(sketch, "E103", {"start": v(1, -225.23) * mm, "end": v(1, -175.23) * mm});
            skLineSegment(sketch, "E104", {"start": v(1, -175.23) * mm, "end": v(0, -173.23) * mm});
            skLineSegment(sketch, "E105", {"start": v(-7, -92.5) * mm, "end": v(-7, -87.5) * mm});
            skLineSegment(sketch, "E106", {"start": v(0, -87.5) * mm, "end": v(-7, -87.5) * mm});
            skSolve(sketch);
        }
        {
            var Q0;
            {var subQ8=sQuery(id+"F24.wireOp",EDGE,"E101.0");Q0=makeQuery(id+"F24.imprint","IMPRINT",FACE,{"disambiguationData":[TD([[makeQuery(id+"F24.imprint","IMPRINT",EDGE,{"derivedFrom":subQ8}),-1.0]])]});}
            var Q1;
            {var subQ9=sQuery(id+"F24.wireOp",EDGE,"E101.2");Q1=makeQuery(id+"F24.imprint","IMPRINT",FACE,{"disambiguationData":[TD([[makeQuery(id+"F24.imprint","IMPRINT",EDGE,{"derivedFrom":subQ9}),-1.0]])]});}
            var Q2;
            {var subQ4=sQuery(id+"F24.wireOp",EDGE,"E102");Q2=makeQuery(id+"F24.imprint","IMPRINT",FACE,{"disambiguationData":[TD([[makeQuery(id+"F24.imprint","IMPRINT",EDGE,{"derivedFrom":subQ4}),1.0]])]});}
            var Q3;
            {var subQ1=sQuery(id+"F24.wireOp",EDGE,"E103");Q3=makeQuery(id+"F24.imprint","IMPRINT",FACE,{"disambiguationData":[TD([[makeQuery(id+"F24.imprint","IMPRINT",EDGE,{"derivedFrom":subQ1}),1.0]])]});}
            var Q4;
            {var subQ0=makeQuery(id+"F22.opExtrude","CAP_EDGE",EDGE,{"disambiguationData":[OSD([sQuery(id+"F21.wireOp",EDGE,"E81"),sQuery(id+"F21.wireOp",EDGE,"E88")])],"isStart":true});var subQ1=sQuery(id+"F24.wireOp",EDGE,"E100");var subQ3=makeQuery(id+"F24.imprint","INTERSECT",VERTEX,{"disambiguationData":[OD(0.0)],"derivedFrom":[subQ0,subQ1]});Q4=makeQuery(id+"F24.imprint","IMPRINT",FACE,{"disambiguationData":[TD([[makeQuery(id+"F24.imprint","IMPRINT",EDGE,{"disambiguationData":[TD([[subQ3,-1.0]])],"derivedFrom":subQ1}),1.0]])]});}
            extrude(context, id + "F25", {"entities" : qUnion([Q0, Q1, Q2, Q3, Q4]), "operationType" : NewBodyOperationType.ADD, "oppositeDirection" : true, "depth" : 5 * mm});
        }
        {
            var Q0;
            {var subQ0=makeQuery(id+"F22.opExtrude","CAP_EDGE",EDGE,{"disambiguationData":[OSD([sQuery(id+"F21.wireOp",EDGE,"E81"),sQuery(id+"F21.wireOp",EDGE,"E88")])],"isStart":true});var subQ1=sQuery(id+"F24.wireOp",EDGE,"E100");var subQ3=makeQuery(id+"F24.imprint","INTERSECT",VERTEX,{"disambiguationData":[OD(0.0)],"derivedFrom":[subQ0,subQ1]});Q0=makeQuery(id+"F24.imprint","IMPRINT",FACE,{"disambiguationData":[TD([[makeQuery(id+"F24.imprint","IMPRINT",EDGE,{"disambiguationData":[TD([[subQ3,-1.0]])],"derivedFrom":subQ1}),1.0]])]});}
            var Q1;
            Q1=makeQuery(id+"F24.imprint","IMPRINT",FACE,{"disambiguationData":[TD([[makeQuery(id+"F24.imprint","IMPRINT",EDGE,{"derivedFrom":sQuery(id+"F24.wireOp",EDGE,"E98")}),-1.0]])]});
            extrude(context, id + "F26", {"entities" : qUnion([Q0, Q1]), "operationType" : NewBodyOperationType.REMOVE, "oppositeDirection" : true, "depth" : 25 * mm});
        }
        {
            var Q0;
            Q0=makeQuery(id+"F6.opExtrude","SWEPT_FACE",FACE,{"disambiguationData":[OSD([sQuery(id+"F5.wireOp",EDGE,"E19")])]});
            var sketch = newSketch(context, id + "F27", { "sketchPlane" : qUnion([Q0])});
            skLineSegment(sketch, "E107.bottom", {"start": v(0, -25) * mm, "end": v(200, -25) * mm, "construction": true});
            skLineSegment(sketch, "E107.top", {"start": v(0, -167.5) * mm, "end": v(200, -167.5) * mm, "construction": true});
            skLineSegment(sketch, "E107.left", {"start": v(0, -25) * mm, "end": v(0, -167.5) * mm, "construction": true});
            skLineSegment(sketch, "E107.right", {"start": v(200, -25) * mm, "end": v(200, -167.5) * mm, "construction": true});
            skLineSegment(sketch, "E108", {"start": v(0, -25) * mm, "end": v(-7, -25) * mm, "construction": true});
            skLineSegment(sketch, "E109", {"start": v(200, -25) * mm, "end": v(207, -25) * mm, "construction": true});
            skLineSegment(sketch, "E110", {"start": v(-7, -25) * mm, "end": v(-7, -48.4) * mm, "construction": true});
            skLineSegment(sketch, "E111", {"start": v(207, -25) * mm, "end": v(207, -51.12) * mm, "construction": true});
            skCircle(sketch, "E112", {"center": v(1, -33) * mm, "radius": 1.5 * mm});
            skCircle(sketch, "E113.cCircle", {"center": v(1, -33) * mm, "radius": 5 * mm, "construction": true});
            skLineSegment(sketch, "E113.0", {"start": v(6, -30.11) * mm, "end": v(6, -35.89) * mm});
            skLineSegment(sketch, "E113.1", {"start": v(6, -35.89) * mm, "end": v(1, -38.77) * mm});
            skLineSegment(sketch, "E113.2", {"start": v(1, -38.77) * mm, "end": v(-4, -35.89) * mm});
            skLineSegment(sketch, "E113.3", {"start": v(-4, -35.89) * mm, "end": v(-4, -30.11) * mm});
            skLineSegment(sketch, "E113.4", {"start": v(-4, -30.11) * mm, "end": v(1, -27.23) * mm});
            skLineSegment(sketch, "E113.5", {"start": v(1, -27.23) * mm, "end": v(6, -30.11) * mm});
            skPoint(sketch, "E113.0.midPoint", {"position": v(6, -33) * mm});
            skCircle(sketch, "E114", {"center": v(199, -33) * mm, "radius": 1.5 * mm});
            skCircle(sketch, "E115.cCircle", {"center": v(199, -33) * mm, "radius": 5 * mm, "construction": true});
            skLineSegment(sketch, "E115.0", {"start": v(194, -35.89) * mm, "end": v(194, -30.11) * mm});
            skLineSegment(sketch, "E115.1", {"start": v(194, -30.11) * mm, "end": v(199, -27.23) * mm});
            skLineSegment(sketch, "E115.2", {"start": v(199, -27.23) * mm, "end": v(204, -30.11) * mm});
            skLineSegment(sketch, "E115.3", {"start": v(204, -30.11) * mm, "end": v(204, -35.89) * mm});
            skLineSegment(sketch, "E115.4", {"start": v(204, -35.89) * mm, "end": v(199, -38.77) * mm});
            skLineSegment(sketch, "E115.5", {"start": v(199, -38.77) * mm, "end": v(194, -35.89) * mm});
            skPoint(sketch, "E115.0.midPoint", {"position": v(194, -33) * mm});
            skLineSegment(sketch, "E116", {"start": v(1, -38.77) * mm, "end": v(0, -39.35) * mm});
            skLineSegment(sketch, "E117", {"start": v(199, -38.77) * mm, "end": v(200, -39.35) * mm});
            skLineSegment(sketch, "E118", {"start": v(1, -27.23) * mm, "end": v(0, -26.65) * mm});
            skLineSegment(sketch, "E119", {"start": v(199, -27.23) * mm, "end": v(200, -26.65) * mm});
            skSolve(sketch);
        }
        {
            var Q0;
            {var subQ8=sQuery(id+"F27.wireOp",EDGE,"E113.3");Q0=makeQuery(id+"F27.imprint","IMPRINT",FACE,{"disambiguationData":[TD([[makeQuery(id+"F27.imprint","IMPRINT",EDGE,{"derivedFrom":subQ8}),-1.0]])]});}
            var Q1;
            Q1=makeQuery(id+"F27.imprint","IMPRINT",FACE,{"disambiguationData":[TD([[makeQuery(id+"F27.imprint","IMPRINT",EDGE,{"derivedFrom":sQuery(id+"F27.wireOp",EDGE,"E113.0")}),-1.0]])]});
            var Q2;
            {var subQ0=makeQuery(id+"F6.opExtrude","CAP_EDGE",EDGE,{"disambiguationData":[OSD([sQuery(id+"F5.wireOp",EDGE,"E19")])],"isStart":true});var subQ1=sQuery(id+"F27.wireOp",EDGE,"E112");var subQ3=makeQuery(id+"F27.imprint","INTERSECT",VERTEX,{"disambiguationData":[OD(0.0)],"derivedFrom":[subQ0,subQ1]});Q2=makeQuery(id+"F27.imprint","IMPRINT",FACE,{"disambiguationData":[TD([[makeQuery(id+"F27.imprint","IMPRINT",EDGE,{"disambiguationData":[TD([[subQ3,-1.0]])],"derivedFrom":subQ1}),1.0]])]});}
            var Q3;
            Q3=makeQuery(id+"F27.imprint","IMPRINT",FACE,{"disambiguationData":[TD([[makeQuery(id+"F27.imprint","IMPRINT",EDGE,{"derivedFrom":sQuery(id+"F27.wireOp",EDGE,"E115.0")}),-1.0]])]});
            var Q4;
            {var subQ0=makeQuery(id+"F6.opExtrude","CAP_EDGE",EDGE,{"disambiguationData":[OSD([sQuery(id+"F5.wireOp",EDGE,"E19")])],"isStart":false});var subQ1=sQuery(id+"F27.wireOp",EDGE,"E114");var subQ3=makeQuery(id+"F27.imprint","INTERSECT",VERTEX,{"disambiguationData":[OD(0.0)],"derivedFrom":[subQ0,subQ1]});Q4=makeQuery(id+"F27.imprint","IMPRINT",FACE,{"disambiguationData":[TD([[makeQuery(id+"F27.imprint","IMPRINT",EDGE,{"disambiguationData":[TD([[subQ3,-1.0]])],"derivedFrom":subQ1}),1.0]])]});}
            var Q5;
            {var subQ8=sQuery(id+"F27.wireOp",EDGE,"E115.3");Q5=makeQuery(id+"F27.imprint","IMPRINT",FACE,{"disambiguationData":[TD([[makeQuery(id+"F27.imprint","IMPRINT",EDGE,{"derivedFrom":subQ8}),-1.0]])]});}
            var Q6;
            {var subQ3=sQuery(id+"F27.wireOp",EDGE,"E117");Q6=makeQuery(id+"F27.imprint","IMPRINT",FACE,{"disambiguationData":[TD([[makeQuery(id+"F27.imprint","IMPRINT",EDGE,{"derivedFrom":subQ3}),1.0]])]});}
            var Q7;
            {var subQ3=sQuery(id+"F27.wireOp",EDGE,"E119");Q7=makeQuery(id+"F27.imprint","IMPRINT",FACE,{"disambiguationData":[TD([[makeQuery(id+"F27.imprint","IMPRINT",EDGE,{"derivedFrom":subQ3}),-1.0]])]});}
            var Q8;
            {var subQ3=sQuery(id+"F27.wireOp",EDGE,"E116");Q8=makeQuery(id+"F27.imprint","IMPRINT",FACE,{"disambiguationData":[TD([[makeQuery(id+"F27.imprint","IMPRINT",EDGE,{"derivedFrom":subQ3}),-1.0]])]});}
            var Q9;
            {var subQ3=sQuery(id+"F27.wireOp",EDGE,"E118");Q9=makeQuery(id+"F27.imprint","IMPRINT",FACE,{"disambiguationData":[TD([[makeQuery(id+"F27.imprint","IMPRINT",EDGE,{"derivedFrom":subQ3}),1.0]])]});}
            extrude(context, id + "F28", {"entities" : qUnion([Q0, Q1, Q2, Q3, Q4, Q5, Q6, Q7, Q8, Q9]), "operationType" : NewBodyOperationType.REMOVE, "oppositeDirection" : true, "depth" : 25 * mm});
        }
        {
            var Q0;
            Q0=makeQuery(id+"F6.opExtrude","SWEPT_FACE",FACE,{"disambiguationData":[OSD([sQuery(id+"F5.wireOp",EDGE,"E19")])]});
            var sketch = newSketch(context, id + "F29", { "sketchPlane" : qUnion([Q0])});
            skLineSegment(sketch, "E120", {"start": v(200, -39.35) * mm, "end": v(194, -35.89) * mm});
            skLineSegment(sketch, "E121", {"start": v(194, -35.89) * mm, "end": v(194, -30.11) * mm});
            skLineSegment(sketch, "E122", {"start": v(194, -30.11) * mm, "end": v(200, -26.65) * mm});
            skLineSegment(sketch, "E123", {"start": v(200, -26.65) * mm, "end": v(200, -1.65) * mm});
            skLineSegment(sketch, "E124", {"start": v(200, -1.65) * mm, "end": v(207, -6.65) * mm});
            skLineSegment(sketch, "E125", {"start": v(207, -6.65) * mm, "end": v(207, -59.35) * mm});
            skLineSegment(sketch, "E126", {"start": v(207, -59.35) * mm, "end": v(200, -64.35) * mm});
            skLineSegment(sketch, "E127", {"start": v(207, -59.35) * mm, "end": v(200, -59.35) * mm, "construction": true});
            skLineSegment(sketch, "E128.0.MirrorCS", {"start": v(206, -30.11) * mm, "end": v(200, -26.65) * mm});
            skLineSegment(sketch, "E128.1.MirrorCS", {"start": v(200, -39.35) * mm, "end": v(206, -35.89) * mm});
            skLineSegment(sketch, "E128.2.MirrorCS", {"start": v(206, -35.89) * mm, "end": v(206, -30.11) * mm});
            skCircle(sketch, "E129", {"center": v(199, -33) * mm, "radius": 1.5 * mm});
            skSolve(sketch);
        }
        {
            var Q0;
            Q0 = qSketchRegion(id + "F29", true);
            extrude(context, id + "F30", {"entities" : qUnion([Q0]), "oppositeDirection" : true, "depth" : 5 * mm});
        }
        {
            var Q0;
            {var subQ3=sQuery(id+"F29.wireOp",EDGE,"E124");Q0=makeQuery(id+"F29.imprint","IMPRINT",FACE,{"disambiguationData":[TD([[makeQuery(id+"F29.imprint","IMPRINT",EDGE,{"derivedFrom":subQ3}),-1.0]])]});}
            extrude(context, id + "F31", {"entities" : qUnion([Q0]), "operationType" : NewBodyOperationType.ADD, "oppositeDirection" : true, "depth" : 25 * mm});
        }
        {
            var Q0;
            Q0=makeQuery(id+"F31.opExtrude","SWEPT_FACE",FACE,{"disambiguationData":[OSD([sQuery(id+"F29.wireOp",EDGE,"E125")])]});
            var sketch = newSketch(context, id + "F32", { "sketchPlane" : qUnion([Q0])});
            skLineSegment(sketch, "E130.bottom", {"start": v(-59.35, 25) * mm, "end": v(-6.65, 25) * mm, "construction": true});
            skLineSegment(sketch, "E130.top", {"start": v(-59.35, 0) * mm, "end": v(-6.65, 0) * mm, "construction": true});
            skLineSegment(sketch, "E130.left", {"start": v(-59.35, 25) * mm, "end": v(-59.35, 0) * mm, "construction": true});
            skLineSegment(sketch, "E130.right", {"start": v(-6.65, 25) * mm, "end": v(-6.65, 0) * mm, "construction": true});
            skCircle(sketch, "E131", {"center": v(-54.35, 20) * mm, "radius": 1.5 * mm});
            skCircle(sketch, "E132", {"center": v(-46.85, 5) * mm, "radius": 1.5 * mm});
            skCircle(sketch, "E133", {"center": v(-19.15, 5) * mm, "radius": 1.5 * mm});
            skCircle(sketch, "E134", {"center": v(-11.65, 20) * mm, "radius": 1.5 * mm});
            skSolve(sketch);
        }
        {
            var Q0;
            Q0 = qSketchRegion(id + "F32", true);
            extrude(context, id + "F33", {"entities" : qUnion([Q0]), "operationType" : NewBodyOperationType.REMOVE, "oppositeDirection" : true, "depth" : 17 * mm});
        }
        {
            var Q0;
            Q0=makeQuery(id+"F31.opExtrude","CAP_FACE",FACE,{"disambiguationData":[OSD([sQuery(id+"F5.wireOp",EDGE,"E19"),sQuery(id+"F29.wireOp",EDGE,"E123"),sQuery(id+"F29.wireOp",EDGE,"E124"),sQuery(id+"F29.wireOp",EDGE,"E125"),sQuery(id+"F29.wireOp",EDGE,"E126"),sQuery(id+"F29.wireOp",EDGE,"E128.0.MirrorCS"),sQuery(id+"F29.wireOp",EDGE,"E128.1.MirrorCS"),sQuery(id+"F29.wireOp",EDGE,"E128.2.MirrorCS")])],"isStart":false});
            var sketch = newSketch(context, id + "F34", { "sketchPlane" : qUnion([Q0])});
            skLineSegment(sketch, "E135", {"start": v(200, 39.35) * mm, "end": v(200, 26.65) * mm});
            skLineSegment(sketch, "E136", {"start": v(200, 39.35) * mm, "end": v(207, 43.4) * mm});
            skLineSegment(sketch, "E137", {"start": v(200, 26.65) * mm, "end": v(207, 22.6) * mm});
            skSolve(sketch);
        }
        {
            var Q0;
            Q0 = qSketchRegion(id + "F34", true);
            var Q1;
            {var subQ2=sQuery(id+"F34.wireOp",EDGE,"E136");Q1=makeQuery(id+"F34.imprint","IMPRINT",FACE,{"disambiguationData":[TD([[makeQuery(id+"F34.imprint","IMPRINT",EDGE,{"derivedFrom":subQ2}),-1.0]])]});}
            extrude(context, id + "F35", {"entities" : qUnion([Q0, Q1]), "operationType" : NewBodyOperationType.REMOVE, "oppositeDirection" : true, "depth" : 20 * mm});
        }
        {
            var Q0;
            Q0=makeQuery(id+"F6.opExtrude","SWEPT_FACE",FACE,{"disambiguationData":[OSD([sQuery(id+"F5.wireOp",EDGE,"E19")])]});
            var sketch = newSketch(context, id + "F36", { "sketchPlane" : qUnion([Q0])});
            skLineSegment(sketch, "E138", {"start": v(0, -26.65) * mm, "end": v(6, -30.11) * mm});
            skLineSegment(sketch, "E139", {"start": v(6, -30.11) * mm, "end": v(6, -35.89) * mm});
            skLineSegment(sketch, "E140", {"start": v(6, -35.89) * mm, "end": v(0, -39.35) * mm});
            skLineSegment(sketch, "E141", {"start": v(0, -39.35) * mm, "end": v(0, -64.35) * mm});
            skLineSegment(sketch, "E142", {"start": v(0, -64.35) * mm, "end": v(-7, -59.35) * mm});
            skLineSegment(sketch, "E143", {"start": v(-7, -59.35) * mm, "end": v(-7, -6.65) * mm});
            skLineSegment(sketch, "E144", {"start": v(-7, -6.65) * mm, "end": v(0, -1.65) * mm});
            skLineSegment(sketch, "E145", {"start": v(0, -1.65) * mm, "end": v(0, -26.65) * mm});
            skLineSegment(sketch, "E146", {"start": v(-7, -59.35) * mm, "end": v(0, -59.35) * mm, "construction": true});
            skLineSegment(sketch, "E147.0.MirrorCS", {"start": v(-6, -35.89) * mm, "end": v(0, -39.35) * mm});
            skLineSegment(sketch, "E147.1.MirrorCS", {"start": v(0, -26.65) * mm, "end": v(-6, -30.11) * mm});
            skLineSegment(sketch, "E147.2.MirrorCS", {"start": v(-6, -30.11) * mm, "end": v(-6, -35.89) * mm});
            skCircle(sketch, "E148", {"center": v(1, -33) * mm, "radius": 1.5 * mm});
            skSolve(sketch);
        }
        {
            var Q0;
            Q0=makeQuery(id+"F36.imprint","IMPRINT",FACE,{"disambiguationData":[TD([[makeQuery(id+"F36.imprint","IMPRINT",EDGE,{"derivedFrom":sQuery(id+"F36.wireOp",EDGE,"E138")}),-1.0]])]});
            var Q1;
            Q1=makeQuery(id+"F36.imprint","IMPRINT",FACE,{"disambiguationData":[TD([[makeQuery(id+"F36.imprint","IMPRINT",EDGE,{"derivedFrom":sQuery(id+"F36.wireOp",EDGE,"E141")}),-1.0]])]});
            extrude(context, id + "F37", {"entities" : qUnion([Q0, Q1]), "oppositeDirection" : true, "depth" : 25 * mm});
        }
        {
            var Q0;
            Q0=makeQuery(id+"F37.opExtrude","SWEPT_FACE",FACE,{"disambiguationData":[OSD([sQuery(id+"F36.wireOp",EDGE,"E143")])]});
            var sketch = newSketch(context, id + "F38", { "sketchPlane" : qUnion([Q0])});
            skLineSegment(sketch, "E149.bottom", {"start": v(6.65, 0) * mm, "end": v(59.35, 0) * mm, "construction": true});
            skLineSegment(sketch, "E149.top", {"start": v(6.65, 25) * mm, "end": v(59.35, 25) * mm, "construction": true});
            skLineSegment(sketch, "E149.left", {"start": v(6.65, 0) * mm, "end": v(6.65, 25) * mm, "construction": true});
            skLineSegment(sketch, "E149.right", {"start": v(59.35, 0) * mm, "end": v(59.35, 25) * mm, "construction": true});
            skCircle(sketch, "E150", {"center": v(11.65, 20) * mm, "radius": 1.5 * mm});
            skCircle(sketch, "E151", {"center": v(19.15, 5) * mm, "radius": 1.5 * mm});
            skCircle(sketch, "E152", {"center": v(46.85, 5) * mm, "radius": 1.5 * mm});
            skCircle(sketch, "E153", {"center": v(54.35, 20) * mm, "radius": 1.5 * mm});
            skSolve(sketch);
        }
        {
            var Q0;
            Q0 = qSketchRegion(id + "F38", true);
            extrude(context, id + "F39", {"entities" : qUnion([Q0]), "operationType" : NewBodyOperationType.REMOVE, "oppositeDirection" : true, "depth" : 17 * mm});
        }
        {
            var Q0;
            Q0=makeQuery(id+"F37.opExtrude","CAP_FACE",FACE,{"disambiguationData":[OSD([sQuery(id+"F36.wireOp",EDGE,"E138"),sQuery(id+"F36.wireOp",EDGE,"E139"),sQuery(id+"F36.wireOp",EDGE,"E140"),sQuery(id+"F36.wireOp",EDGE,"E141"),sQuery(id+"F36.wireOp",EDGE,"E142"),sQuery(id+"F36.wireOp",EDGE,"E143"),sQuery(id+"F36.wireOp",EDGE,"E144"),sQuery(id+"F36.wireOp",EDGE,"E145"),sQuery(id+"F36.wireOp",EDGE,"b36e4456-db93-474d-aa25-f5c221016a51")])],"isStart":false});
            var sketch = newSketch(context, id + "F40", { "sketchPlane" : qUnion([Q0])});
            skLineSegment(sketch, "E154", {"start": v(0, 39.35) * mm, "end": v(6, 35.89) * mm});
            skLineSegment(sketch, "E155", {"start": v(6, 35.89) * mm, "end": v(6, 30.11) * mm});
            skLineSegment(sketch, "E156", {"start": v(6, 30.11) * mm, "end": v(0, 26.65) * mm});
            skLineSegment(sketch, "E157", {"start": v(0, 26.65) * mm, "end": v(-7, 22.6) * mm});
            skLineSegment(sketch, "E158", {"start": v(-7, 22.6) * mm, "end": v(-7, 43.4) * mm});
            skLineSegment(sketch, "E159", {"start": v(-7, 43.4) * mm, "end": v(0, 39.35) * mm});
            skSolve(sketch);
        }
        {
            var Q0;
            Q0 = qSketchRegion(id + "F40", true);
            extrude(context, id + "F41", {"entities" : qUnion([Q0]), "operationType" : NewBodyOperationType.REMOVE, "oppositeDirection" : true, "depth" : 20 * mm});
        }
    });
